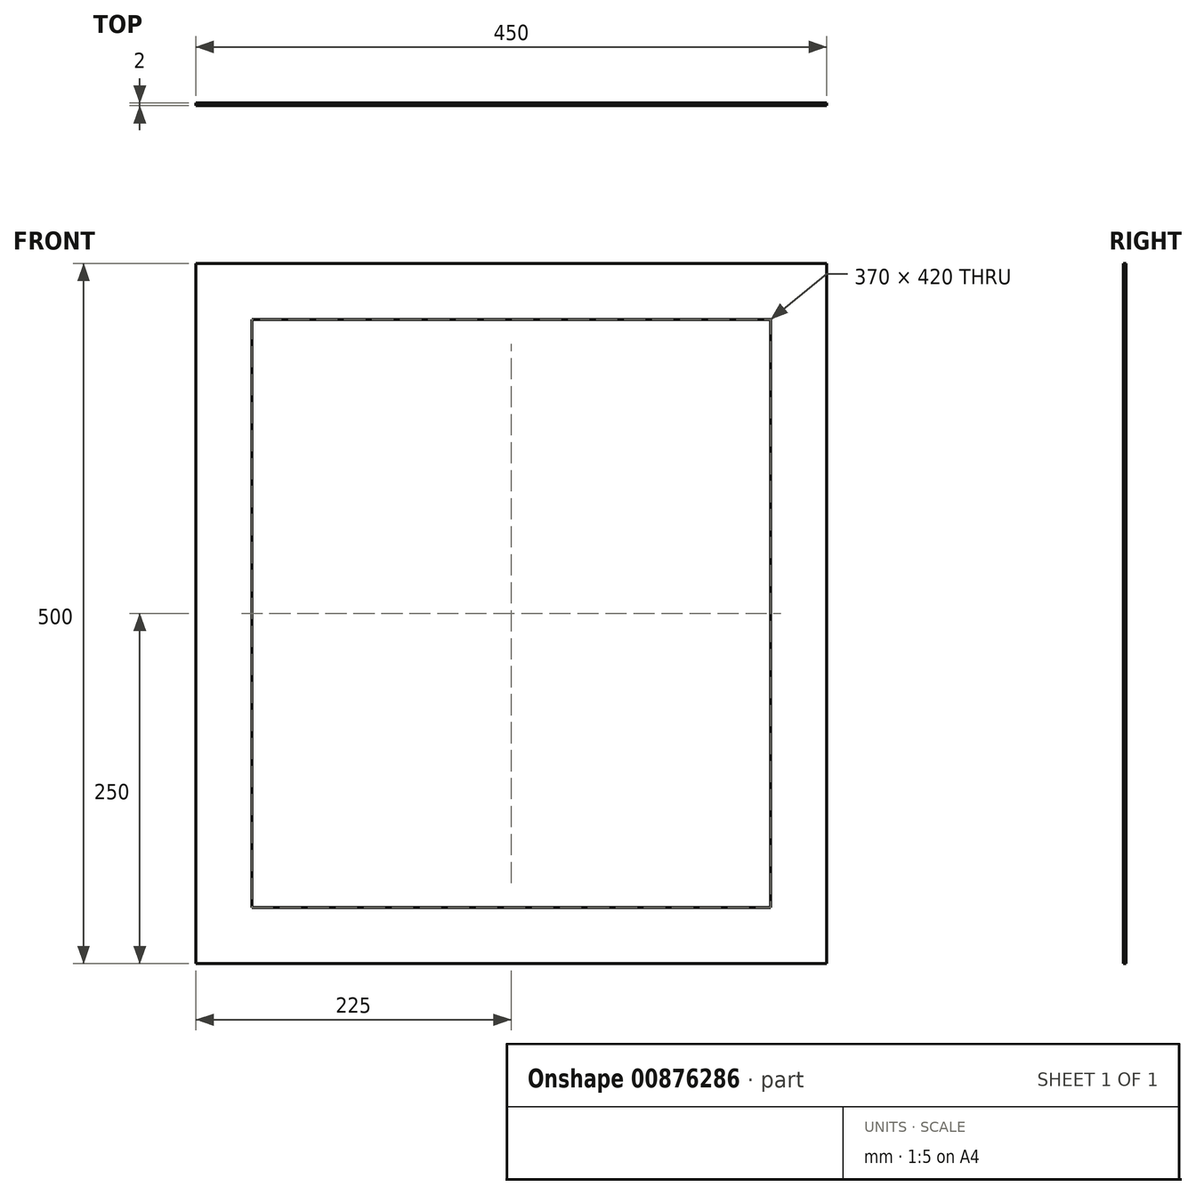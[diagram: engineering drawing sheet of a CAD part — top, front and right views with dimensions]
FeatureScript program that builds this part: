
annotation { "Feature Type Name" : "Feature", "Feature Type Description" : "" }
export const myFeature = defineFeature(function(context is Context, id is Id, definition is map)
    precondition{}
    {
        {
            var Q0;
            Q0=qCreatedBy(makeId("Front.planeOp"),FACE);
            var sketch = newSketch(context, id + "F0", { "sketchPlane" : qUnion([Q0])});
            skPoint(sketch, "E0.middle", {"position": v(0, 0) * mm});
            skLineSegment(sketch, "E1.0", {"start": v(-185, 285) * mm, "end": v(185, 285) * mm});
            skLineSegment(sketch, "E1.1", {"start": v(-185, 285) * mm, "end": v(-185, -135) * mm});
            skLineSegment(sketch, "E1.2", {"start": v(-185, -135) * mm, "end": v(185, -135) * mm});
            skLineSegment(sketch, "E1.3", {"start": v(185, 285) * mm, "end": v(185, -135) * mm});
            skLineSegment(sketch, "E2.0", {"start": v(-225, 325) * mm, "end": v(225, 325) * mm});
            skLineSegment(sketch, "E2.1", {"start": v(-225, 325) * mm, "end": v(-225, -175) * mm});
            skLineSegment(sketch, "E2.2", {"start": v(-225, -175) * mm, "end": v(225, -175) * mm});
            skLineSegment(sketch, "E2.3", {"start": v(225, 325) * mm, "end": v(225, -175) * mm});
            skSolve(sketch);
        }
        {
            var Q0;
            Q0=makeQuery(id+"F0.imprint","IMPRINT",FACE,{"disambiguationData":[TD([[makeQuery(id+"F0.imprint","IMPRINT",EDGE,{"derivedFrom":sQuery(id+"F0.wireOp",EDGE,"E1.0")}),1.0]])]});
            extrude(context, id + "F1", {"entities" : qUnion([Q0]), "depth" : 2 * mm, "offsetDistance" : 25.4 * mm});
        }
    });
